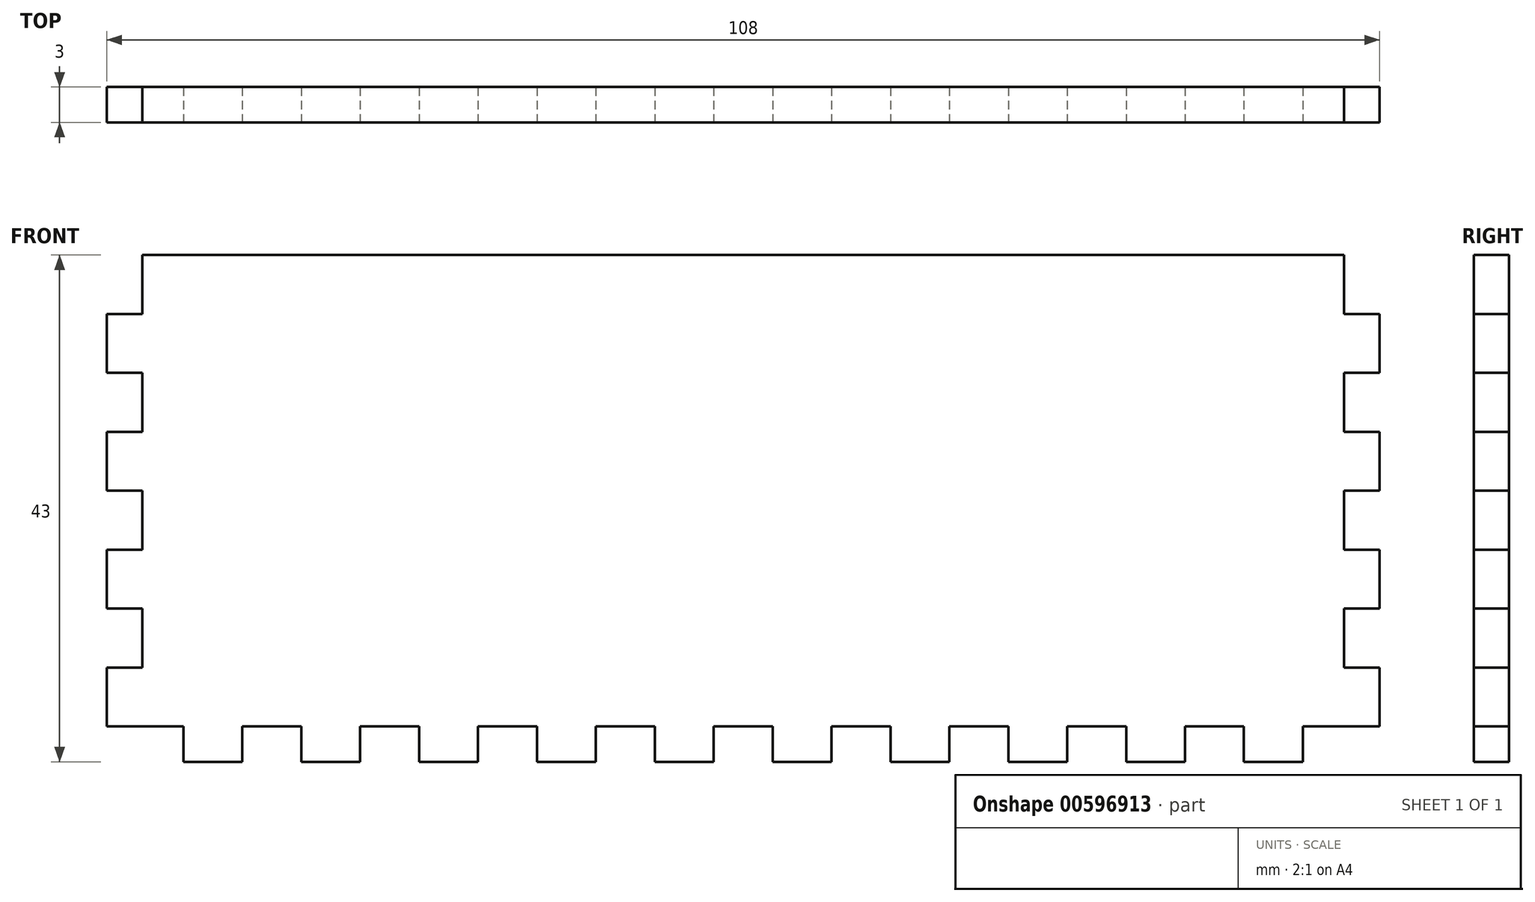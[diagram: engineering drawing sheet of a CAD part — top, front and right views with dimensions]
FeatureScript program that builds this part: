
annotation { "Feature Type Name" : "Feature", "Feature Type Description" : "" }
export const myFeature = defineFeature(function(context is Context, id is Id, definition is map)
    precondition{}
    {
        {
            var Q0;
            Q0=qCreatedBy(makeId("Front.planeOp"),FACE);
            var sketch = newSketch(context, id + "F0", { "sketchPlane" : qUnion([Q0])});
            skLineSegment(sketch, "E0.bottom", {"start": v(51, 20) * mm, "end": v(-51, 20) * mm});
            skLineSegment(sketch, "E0.top", {"start": v(51, -20) * mm, "end": v(-51, -20) * mm});
            skLineSegment(sketch, "E0.left", {"start": v(51, 20) * mm, "end": v(51, -20) * mm});
            skLineSegment(sketch, "E0.right", {"start": v(-51, 20) * mm, "end": v(-51, -20) * mm});
            skPoint(sketch, "E0.middle", {"position": v(0, 0) * mm});
            skSolve(sketch);
        }
        {
            var Q0;
            Q0 = qSketchRegion(id + "F0", true);
            extrude(context, id + "F1", {"entities" : qUnion([Q0]), "depth" : 3 * mm, "offsetDistance" : 25 * mm});
        }
        {
            var Q0;
            Q0=makeQuery(id+"F1.opExtrude","CAP_FACE",FACE,{"disambiguationData":[OSD([sQuery(id+"F0.wireOp",EDGE,"E0.bottom"),sQuery(id+"F0.wireOp",EDGE,"E0.top"),sQuery(id+"F0.wireOp",EDGE,"E0.left"),sQuery(id+"F0.wireOp",EDGE,"E0.right")])],"isStart":false});
            var sketch = newSketch(context, id + "F2", { "sketchPlane" : qUnion([Q0])});
            skLineSegment(sketch, "E1.bottom", {"start": v(-51, -20) * mm, "end": v(-54, -20) * mm});
            skLineSegment(sketch, "E1.top", {"start": v(-51, -15) * mm, "end": v(-54, -15) * mm});
            skLineSegment(sketch, "E1.left", {"start": v(-51, -20) * mm, "end": v(-51, -15) * mm});
            skLineSegment(sketch, "E1.right", {"start": v(-54, -20) * mm, "end": v(-54, -15) * mm});
            skLineSegment(sketch, "E2.0.1.0", {"start": v(-51, -5) * mm, "end": v(-54, -5) * mm});
            skLineSegment(sketch, "E2.0.1.1", {"start": v(-54, -10) * mm, "end": v(-54, -5) * mm});
            skLineSegment(sketch, "E2.0.1.2", {"start": v(-51, -10) * mm, "end": v(-51, -5) * mm});
            skLineSegment(sketch, "E2.0.1.3", {"start": v(-51, -10) * mm, "end": v(-54, -10) * mm});
            skLineSegment(sketch, "E2.0.2.0", {"start": v(-51, 5) * mm, "end": v(-54, 5) * mm});
            skLineSegment(sketch, "E2.0.2.1", {"start": v(-54, 0) * mm, "end": v(-54, 5) * mm});
            skLineSegment(sketch, "E2.0.2.2", {"start": v(-51, 0) * mm, "end": v(-51, 5) * mm});
            skLineSegment(sketch, "E2.0.2.3", {"start": v(-51, 0) * mm, "end": v(-54, 0) * mm});
            skLineSegment(sketch, "E2.0.3.0", {"start": v(-51, 15) * mm, "end": v(-54, 15) * mm});
            skLineSegment(sketch, "E2.0.3.1", {"start": v(-54, 10) * mm, "end": v(-54, 15) * mm});
            skLineSegment(sketch, "E2.0.3.2", {"start": v(-51, 10) * mm, "end": v(-51, 15) * mm});
            skLineSegment(sketch, "E2.0.3.3", {"start": v(-51, 10) * mm, "end": v(-54, 10) * mm});
            skLineSegment(sketch, "E2.direction1", {"start": v(-54, -15) * mm, "end": v(-29, -15) * mm, "construction": true});
            skLineSegment(sketch, "E2.direction2", {"start": v(-54, -15) * mm, "end": v(-54, -5) * mm, "construction": true});
            skLineSegment(sketch, "E3.MirrorCS", {"start": v(54, -10) * mm, "end": v(54, -5) * mm});
            skLineSegment(sketch, "E4.MirrorCS", {"start": v(51, -5) * mm, "end": v(54, -5) * mm});
            skLineSegment(sketch, "E5.MirrorCS", {"start": v(51, -20) * mm, "end": v(51, -15) * mm});
            skLineSegment(sketch, "E6.MirrorCS", {"start": v(54, 10) * mm, "end": v(54, 15) * mm});
            skLineSegment(sketch, "E7.MirrorCS", {"start": v(51, -20) * mm, "end": v(54, -20) * mm});
            skLineSegment(sketch, "E8.MirrorCS", {"start": v(51, -15) * mm, "end": v(54, -15) * mm});
            skLineSegment(sketch, "E9.MirrorCS", {"start": v(54, -20) * mm, "end": v(54, -15) * mm});
            skLineSegment(sketch, "E10.MirrorCS", {"start": v(51, 15) * mm, "end": v(54, 15) * mm});
            skLineSegment(sketch, "E11.MirrorCS", {"start": v(51, 10) * mm, "end": v(54, 10) * mm});
            skLineSegment(sketch, "E12.MirrorCS", {"start": v(54, -15) * mm, "end": v(54, -5) * mm, "construction": true});
            skLineSegment(sketch, "E13.MirrorCS", {"start": v(51, 10) * mm, "end": v(51, 15) * mm});
            skLineSegment(sketch, "E14.MirrorCS", {"start": v(54, 0) * mm, "end": v(54, 5) * mm});
            skLineSegment(sketch, "E15.MirrorCS", {"start": v(51, 0) * mm, "end": v(51, 5) * mm});
            skLineSegment(sketch, "E16.MirrorCS", {"start": v(51, 0) * mm, "end": v(54, 0) * mm});
            skLineSegment(sketch, "E17.MirrorCS", {"start": v(51, -10) * mm, "end": v(51, -5) * mm});
            skLineSegment(sketch, "E18.MirrorCS", {"start": v(51, -10) * mm, "end": v(54, -10) * mm});
            skLineSegment(sketch, "E19.MirrorCS", {"start": v(51, 5) * mm, "end": v(54, 5) * mm});
            skSolve(sketch);
        }
        {
            var Q0;
            Q0 = qSketchRegion(id + "F2", true);
            extrude(context, id + "F3", {"entities" : qUnion([Q0]), "operationType" : NewBodyOperationType.ADD, "oppositeDirection" : true, "depth" : 3 * mm, "offsetDistance" : 25 * mm});
        }
        {
            var Q0;
            Q0=makeQuery(id+"F3.boolean.opBoolean","MERGE",FACE,{"derivedFrom":[makeQuery(id+"F1.opExtrude","CAP_FACE",FACE,{"disambiguationData":[OSD([sQuery(id+"F0.wireOp",EDGE,"E0.bottom"),sQuery(id+"F0.wireOp",EDGE,"E0.top"),sQuery(id+"F0.wireOp",EDGE,"E0.left"),sQuery(id+"F0.wireOp",EDGE,"E0.right")])],"isStart":false}),makeQuery(id+"F3.opExtrude","CAP_FACE",FACE,{"disambiguationData":[OSD([sQuery(id+"F2.wireOp",EDGE,"E1.bottom"),sQuery(id+"F2.wireOp",EDGE,"E1.top"),sQuery(id+"F2.wireOp",EDGE,"E1.left"),sQuery(id+"F2.wireOp",EDGE,"E1.right")])],"isStart":true}),makeQuery(id+"F3.opExtrude","CAP_FACE",FACE,{"disambiguationData":[OSD([sQuery(id+"F2.wireOp",EDGE,"E2.0.1.0"),sQuery(id+"F2.wireOp",EDGE,"E2.0.1.1"),sQuery(id+"F2.wireOp",EDGE,"E2.0.1.2"),sQuery(id+"F2.wireOp",EDGE,"E2.0.1.3")])],"isStart":true}),makeQuery(id+"F3.opExtrude","CAP_FACE",FACE,{"disambiguationData":[OSD([sQuery(id+"F2.wireOp",EDGE,"E2.0.2.0"),sQuery(id+"F2.wireOp",EDGE,"E2.0.2.1"),sQuery(id+"F2.wireOp",EDGE,"E2.0.2.2"),sQuery(id+"F2.wireOp",EDGE,"E2.0.2.3")])],"isStart":true}),makeQuery(id+"F3.opExtrude","CAP_FACE",FACE,{"disambiguationData":[OSD([sQuery(id+"F2.wireOp",EDGE,"E2.0.3.0"),sQuery(id+"F2.wireOp",EDGE,"E2.0.3.1"),sQuery(id+"F2.wireOp",EDGE,"E2.0.3.2"),sQuery(id+"F2.wireOp",EDGE,"E2.0.3.3")])],"isStart":true}),makeQuery(id+"F3.opExtrude","CAP_FACE",FACE,{"disambiguationData":[OSD([sQuery(id+"F2.wireOp",EDGE,"E3.MirrorCS"),sQuery(id+"F2.wireOp",EDGE,"E4.MirrorCS"),sQuery(id+"F2.wireOp",EDGE,"E17.MirrorCS"),sQuery(id+"F2.wireOp",EDGE,"E18.MirrorCS")])],"isStart":true}),makeQuery(id+"F3.opExtrude","CAP_FACE",FACE,{"disambiguationData":[OSD([sQuery(id+"F2.wireOp",EDGE,"E5.MirrorCS"),sQuery(id+"F2.wireOp",EDGE,"E7.MirrorCS"),sQuery(id+"F2.wireOp",EDGE,"E8.MirrorCS"),sQuery(id+"F2.wireOp",EDGE,"E9.MirrorCS")])],"isStart":true}),makeQuery(id+"F3.opExtrude","CAP_FACE",FACE,{"disambiguationData":[OSD([sQuery(id+"F2.wireOp",EDGE,"E6.MirrorCS"),sQuery(id+"F2.wireOp",EDGE,"E10.MirrorCS"),sQuery(id+"F2.wireOp",EDGE,"E11.MirrorCS"),sQuery(id+"F2.wireOp",EDGE,"E13.MirrorCS")])],"isStart":true}),makeQuery(id+"F3.opExtrude","CAP_FACE",FACE,{"disambiguationData":[OSD([sQuery(id+"F2.wireOp",EDGE,"E14.MirrorCS"),sQuery(id+"F2.wireOp",EDGE,"E15.MirrorCS"),sQuery(id+"F2.wireOp",EDGE,"E16.MirrorCS"),sQuery(id+"F2.wireOp",EDGE,"E19.MirrorCS")])],"isStart":true})]});
            var sketch = newSketch(context, id + "F4", { "sketchPlane" : qUnion([Q0])});
            skLineSegment(sketch, "E20", {"start": v(0, -20) * mm, "end": v(0, -23) * mm, "construction": true});
            skPoint(sketch, "E20.endSnap0", {"position": v(0, -20) * mm});
            skLineSegment(sketch, "E21", {"start": v(0, -23) * mm, "end": v(2.5, -23) * mm, "construction": true});
            skLineSegment(sketch, "E22.bottom", {"start": v(2.5, -23) * mm, "end": v(7.5, -23) * mm});
            skLineSegment(sketch, "E22.top", {"start": v(2.5, -20) * mm, "end": v(7.5, -20) * mm});
            skLineSegment(sketch, "E22.left", {"start": v(2.5, -23) * mm, "end": v(2.5, -20) * mm});
            skLineSegment(sketch, "E22.right", {"start": v(7.5, -23) * mm, "end": v(7.5, -20) * mm});
            skLineSegment(sketch, "E23.1.0.0", {"start": v(12.5, -23) * mm, "end": v(17.5, -23) * mm});
            skLineSegment(sketch, "E23.1.0.1", {"start": v(12.5, -23) * mm, "end": v(12.5, -20) * mm});
            skLineSegment(sketch, "E23.1.0.2", {"start": v(17.5, -23) * mm, "end": v(17.5, -20) * mm});
            skLineSegment(sketch, "E23.1.0.3", {"start": v(12.5, -20) * mm, "end": v(17.5, -20) * mm});
            skLineSegment(sketch, "E23.2.0.0", {"start": v(22.5, -23) * mm, "end": v(27.5, -23) * mm});
            skLineSegment(sketch, "E23.2.0.1", {"start": v(22.5, -23) * mm, "end": v(22.5, -20) * mm});
            skLineSegment(sketch, "E23.2.0.2", {"start": v(27.5, -23) * mm, "end": v(27.5, -20) * mm});
            skLineSegment(sketch, "E23.2.0.3", {"start": v(22.5, -20) * mm, "end": v(27.5, -20) * mm});
            skLineSegment(sketch, "E23.3.0.0", {"start": v(32.5, -23) * mm, "end": v(37.5, -23) * mm});
            skLineSegment(sketch, "E23.3.0.1", {"start": v(32.5, -23) * mm, "end": v(32.5, -20) * mm});
            skLineSegment(sketch, "E23.3.0.2", {"start": v(37.5, -23) * mm, "end": v(37.5, -20) * mm});
            skLineSegment(sketch, "E23.3.0.3", {"start": v(32.5, -20) * mm, "end": v(37.5, -20) * mm});
            skLineSegment(sketch, "E23.4.0.0", {"start": v(42.5, -23) * mm, "end": v(47.5, -23) * mm});
            skLineSegment(sketch, "E23.4.0.1", {"start": v(42.5, -23) * mm, "end": v(42.5, -20) * mm});
            skLineSegment(sketch, "E23.4.0.2", {"start": v(47.5, -23) * mm, "end": v(47.5, -20) * mm});
            skLineSegment(sketch, "E23.4.0.3", {"start": v(42.5, -20) * mm, "end": v(47.5, -20) * mm});
            skLineSegment(sketch, "E23.direction1", {"start": v(2.5, -23) * mm, "end": v(12.5, -23) * mm, "construction": true});
            skLineSegment(sketch, "E24.MirrorCS", {"start": v(-27.5, -23) * mm, "end": v(-27.5, -20) * mm});
            skLineSegment(sketch, "E25.MirrorCS", {"start": v(-22.5, -23) * mm, "end": v(-22.5, -20) * mm});
            skLineSegment(sketch, "E26.MirrorCS", {"start": v(-17.5, -23) * mm, "end": v(-17.5, -20) * mm});
            skLineSegment(sketch, "E27.MirrorCS", {"start": v(-12.5, -23) * mm, "end": v(-12.5, -20) * mm});
            skLineSegment(sketch, "E28.MirrorCS", {"start": v(-7.5, -23) * mm, "end": v(-7.5, -20) * mm});
            skLineSegment(sketch, "E29.MirrorCS", {"start": v(-2.5, -23) * mm, "end": v(-2.5, -20) * mm});
            skLineSegment(sketch, "E30.MirrorCS", {"start": v(-32.5, -23) * mm, "end": v(-32.5, -20) * mm});
            skLineSegment(sketch, "E31.MirrorCS", {"start": v(-47.5, -23) * mm, "end": v(-47.5, -20) * mm});
            skLineSegment(sketch, "E32.MirrorCS", {"start": v(-37.5, -23) * mm, "end": v(-37.5, -20) * mm});
            skLineSegment(sketch, "E33.MirrorCS", {"start": v(-42.5, -23) * mm, "end": v(-42.5, -20) * mm});
            skLineSegment(sketch, "E34.MirrorCS", {"start": v(-2.5, -23) * mm, "end": v(-7.5, -23) * mm});
            skLineSegment(sketch, "E35.MirrorCS", {"start": v(-32.5, -20) * mm, "end": v(-37.5, -20) * mm});
            skLineSegment(sketch, "E36.MirrorCS", {"start": v(-42.5, -20) * mm, "end": v(-47.5, -20) * mm});
            skLineSegment(sketch, "E37.MirrorCS", {"start": v(-22.5, -23) * mm, "end": v(-27.5, -23) * mm});
            skLineSegment(sketch, "E38.MirrorCS", {"start": v(-12.5, -20) * mm, "end": v(-17.5, -20) * mm});
            skLineSegment(sketch, "E39.MirrorCS", {"start": v(-12.5, -23) * mm, "end": v(-17.5, -23) * mm});
            skLineSegment(sketch, "E40.MirrorCS", {"start": v(-2.5, -20) * mm, "end": v(-7.5, -20) * mm});
            skLineSegment(sketch, "E41.MirrorCS", {"start": v(-32.5, -23) * mm, "end": v(-37.5, -23) * mm});
            skLineSegment(sketch, "E42.MirrorCS", {"start": v(-22.5, -20) * mm, "end": v(-27.5, -20) * mm});
            skLineSegment(sketch, "E43.MirrorCS", {"start": v(-42.5, -23) * mm, "end": v(-47.5, -23) * mm});
            skLineSegment(sketch, "E44.MirrorCS", {"start": v(-2.5, -23) * mm, "end": v(-12.5, -23) * mm, "construction": true});
            skSolve(sketch);
        }
        {
            var Q0;
            Q0 = qSketchRegion(id + "F4", true);
            extrude(context, id + "F5", {"entities" : qUnion([Q0]), "operationType" : NewBodyOperationType.ADD, "oppositeDirection" : true, "depth" : 3 * mm, "offsetDistance" : 25 * mm});
        }
    });
